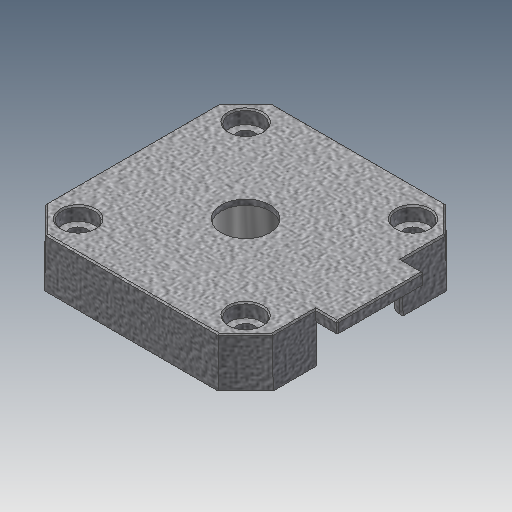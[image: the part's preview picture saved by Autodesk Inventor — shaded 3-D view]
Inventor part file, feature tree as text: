
AUTODESK INVENTOR PART (.ipt)
format: ipt  version: 2020.2 (Build 242310000, 310)  size: 433,664 bytes
history: native  units: mm
features: sketch x13, extrude x11, chamfer x4, fillet x3, projected_geometry x3, hole x2, pattern_circular x1
ambient origin geometry x8: Origin, YZ Plane, XZ Plane, XY Plane, X Axis, Y Axis, Z Axis, Center Point
bodies: Body1 (feature_tree)
feature tree (37):
  extrude  "Extrusion7"  Depth=5.0mm
  extrude  "Extrusion9"  Depth=5.0mm
  extrude  "Extrusion10"  Depth=5.0mm
  extrude  "Extrusion11"  Depth=5.0mm
  extrude  "Extrusion12"  Depth=9.0mm
  hole  "Hole6"  [1 undecoded]
  chamfer  "Chamfer1"  Distance=7.0mm
  chamfer  "Chamfer2"  Distance=1.0mm
  hole  "Hole7"  [1 undecoded]
  extrude  "Extrusion13"  Depth=0.75mm TaperAngle=0.0deg
  extrude  "Extrusion14"  Depth=8.8mm
  pattern_circular  "Circular Pattern1"  [2 undecoded]
  extrude  "Extrusion15"  Depth=1.0mm TaperAngle=0.0deg
  extrude  "Extrusion16"  Depth=1.0mm TaperAngle=0.0deg
  extrude  "Extrusion17"  Depth=2.0mm TaperAngle=360.0deg
  extrude  "Extrusion18"  Depth=2.0mm
  fillet  "Fillet8"  Radius=16.0mm
  chamfer  "Chamfer3"  Distance=21.0mm
  fillet  "Fillet9"  Radius=3.0mm
  fillet  "Fillet10"  Radius=3.0mm
  chamfer  "Chamfer4"  Distance=3.0mm
  sketch  "Sketch11"  dims[d82=42.0mm d83=5.0mm]
  sketch  "Sketch13"  dims[d84=5.0mm d85=5.0mm]
  sketch  "Sketch14"  dims[d86=5.0mm d87=5.0mm]
  projected_geometry  "Projected Loop3"
  sketch  "Sketch15"  dims[d88=5.0mm d89=5.0mm]
  sketch  "Sketch17"  dims[d90=5.0mm d91=9.0mm d92=0.174533mm]
  sketch  "Sketch18"  dims[d96=26.0mm d97=39.0mm d98=7.0mm d99=0.0mm d100=1.0mm d101=0.0mm]
  sketch  "Sketch19"  dims[d102=16.0mm d103=8.25mm d104=0.0mm]
  sketch  "Sketch20"  dims[d112=12.0mm d113=0.75mm d114=0.0mm]
  sketch  "Sketch21"  dims[d115=31.0mm]
  projected_geometry  "Projected Loop4"
  sketch  "Sketch22"  dims[d116=3.4mm d117=6.0mm d118=6.0mm d119=2.5mm d120=90.0deg d121=8.8mm d122=20.594885mm d124=31.0mm]
  sketch  "Sketch23"  dims[d125=0.25mm d126=1.0mm d127=45.0deg]
  projected_geometry  "Projected Loop5"
  sketch  "Sketch24"  dims[d128=0.25mm d129=1.0mm d130=45.0deg]
  sketch  "Sketch25"  dims[d131=9.0mm d132=6.0mm d133=6.0mm d134=2.5mm d135=14.3117mm d136=8.0mm d137=20.594885mm d138=5.0mm d139=1.0mm d140=0.0mm d141=1.0mm d142=0.0mm d143=40.0mm d144=360.0deg d146=4.0mm d147=16.0mm d148=21.0mm d149=3.0mm d150=0.0mm d151=3.0mm d152=0.0mm d153=3.0mm d154=0.0mm d155=7.0mm d156=14.0mm d157=1.0mm d158=1.8mm d159=0.0mm d160=0.5mm d161=0.25mm d162=2.0mm d163=45.0deg d164=2.0mm d165=2.0mm d166=0.25mm d167=2.0mm d168=45.0deg]
note: 4 required parameter values undecoded (feature->parameter linkage not recoverable at this tier; creation-order binding heuristic only, values carry confidence <= 0.55)
